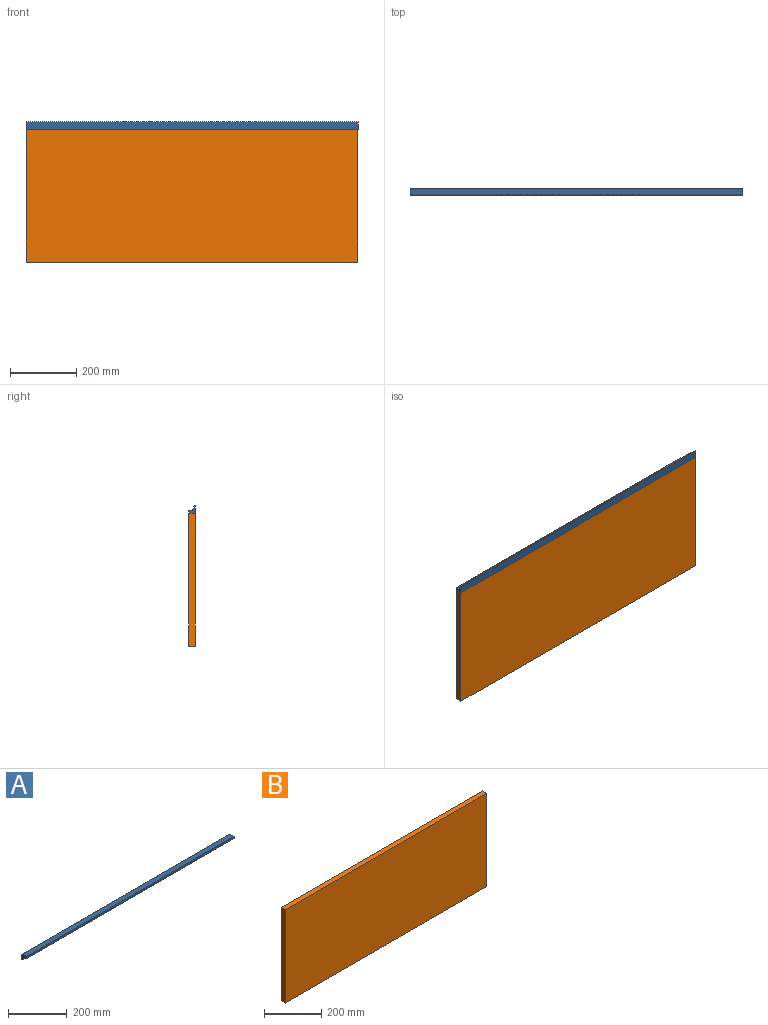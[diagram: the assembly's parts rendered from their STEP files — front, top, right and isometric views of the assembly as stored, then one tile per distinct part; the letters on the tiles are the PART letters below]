
ASSEMBLY  parts=2 mates=1
PART A: 8 faces, bbox 1000x20x22.5 mm
  f0: plane 1000x22.47mm, normal (0,1,0), area 22471.9mm2, adj f1,f5,f6,f7
  f1: plane 1000x20mm, normal (0,0,1), area 20000mm2, adj f0,f2,f6,f7
  f2: plane 1000x8.99mm, normal (0,-1,0), area 8988.8mm2, adj f1,f3,f6,f7
  f3: plane 1000x11.01mm, normal (0,0,-1), area 11011.2mm2, adj f2,f4,f6,f7
  f4: plane 1000x13.48mm, normal (0,-0.91,-0.42), area 14879.1mm2, adj f3,f5,f6,f7
  f5: plane 1000x2.7mm, normal (0,0,-1), area 2696.6mm2, adj f0,f4,f6,f7
  f6: plane 22.47x20mm, normal (1,0,0), area 258.6mm2, adj f0,f1,f2,f3,f4,f5
  f7: plane 22.47x20mm, normal (-1,0,0), area 258.6mm2, adj f0,f1,f2,f3,f4,f5
PART B: 6 faces, bbox 1000x20x400 mm
  f0: plane 400x20mm, normal (-1,0,0), area 8000mm2, adj f1,f3,f4,f5
  f1: plane 1000x20mm, normal (0,0,-1), area 20000mm2, adj f0,f2,f4,f5
  f2: plane 400x20mm, normal (1,0,0), area 8000mm2, adj f1,f3,f4,f5
  f3: plane 1000x20mm, normal (0,0,1), area 20000mm2, adj f0,f2,f4,f5
  f4: plane 1000x400mm, normal (0,-1,0), area 400000mm2, adj f0,f1,f2,f3
  f5: plane 1000x400mm, normal (0,1,0), area 400000mm2, adj f0,f1,f2,f3
PLACE A rot(axis=(-1,0,0),180deg) t=(-618.99,-145.43,90.53)mm
PLACE B t=(-118.99,-135.43,-120.71)mm
MATE planar B.f2 <-> B.f2  axis (1,0,0) through (381.01,-155.43,79.29)mm
